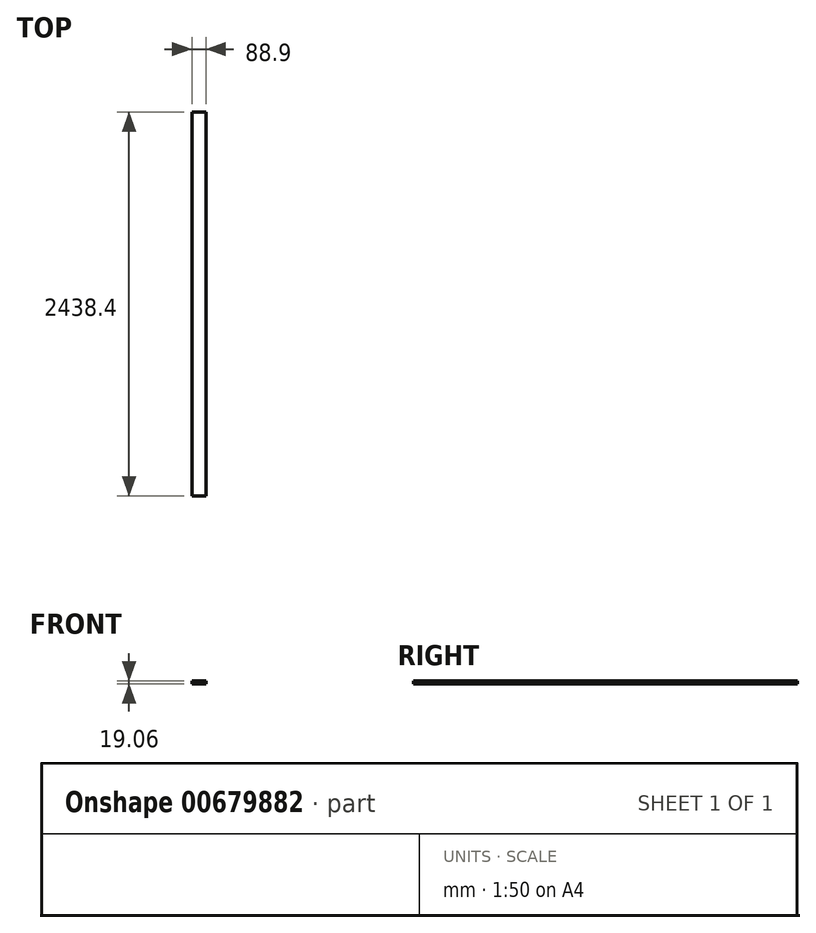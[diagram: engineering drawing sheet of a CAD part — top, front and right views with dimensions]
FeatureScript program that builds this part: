
annotation { "Feature Type Name" : "Feature", "Feature Type Description" : "" }
export const myFeature = defineFeature(function(context is Context, id is Id, definition is map)
    precondition{}
    {
        {
            var Q0;
            Q0=qCreatedBy(makeId("Front.planeOp"),FACE);
            var sketch = newSketch(context, id + "F0", { "sketchPlane" : qUnion([Q0])});
            skLineSegment(sketch, "E0.bottom", {"start": v(-44.45, 9.52) * mm, "end": v(44.45, 9.52) * mm});
            skLineSegment(sketch, "E0.top", {"start": v(-44.45, -9.52) * mm, "end": v(44.45, -9.52) * mm});
            skLineSegment(sketch, "E0.left", {"start": v(-44.45, 9.52) * mm, "end": v(-44.45, -9.52) * mm});
            skLineSegment(sketch, "E0.right", {"start": v(44.45, 9.52) * mm, "end": v(44.45, -9.52) * mm});
            skPoint(sketch, "E0.middle", {"position": v(0, 0) * mm});
            skSolve(sketch);
        }
        {
            var Q0;
            Q0 = qSketchRegion(id + "F0", true);
            extrude(context, id + "F1", {"entities" : qUnion([Q0]), "endBound" : BoundingType.SYMMETRIC, "depth" : 2438.4 * mm, "offsetDistance" : 25.4 * mm});
        }
    });
